# Revit family: BRITUBE LINEAR LIGHT
name_source: partatom
category: Lighting Fixtures
units: mm (PartAtom-declared; Revit-internal decimal feet)

## family parameters
Cut with Voids When Loaded = No
Host = Face
Light Source = Yes
Part Type = Normal
Room Calculation Point = No
Round Connector Dimension = Use Diameter
Shared = No

## types (3) — shared parameters
Apparent Load = 0 VA
Average life based on 77F(HRS) = 50000
CRI = >80
Color Filter = 16777215
Default Elevation = 0' - 0"
Description = The Britube linear fixture features in streamline tube shape with aluminum base and frosted polycar-
bonate lens. It is designed to deliver direct and indirect lighting to commercial spaces.
Dimming / Control = 0-10 V
Dimming Lamp Color Temperature Shift = <None>
Finish/Color = White Aluminum
IP Rating = 20
Inside Body Material = Glasss
Load Classification = Lighting
Manufacturer = Above All Lighting
Power Factor = 1
Suspender Height = 5' - 0"
Tilt Angle = -90.00°
Type Comments = BRITUBE LINEAR LIGHT
URL = https://www.abovealllighting.com
Voltage = 120-347 V

## per-type parameters (varying)
| type | B | Fixture Length | Model | Order number | Photometric Web File | Wattage Comments |
| BIT12ID40SW-35-8 | 1' - 6 19/32" | 3' - 11 3/16" | BIT12ID40SW8 | 16147 | BIT12ID40SW8_(3500K) (1).ies | 40 W |
| BIT24ID80SW8 | 3' - 6" | 7' - 10 1/32" | BIT12ID80SW8 | 16149 | generic | 80 W |
| BIT12ID40SW-40-8 | 1' - 6 19/32" | 3' - 11 3/16" | BIT12ID40SW8 | 16147 | BIT12ID40SW8_(4000K).ies | 40 W |

## geometry (parser evidence)
native form markers: Sweep x4
no freeform markers — native parametric forms only
